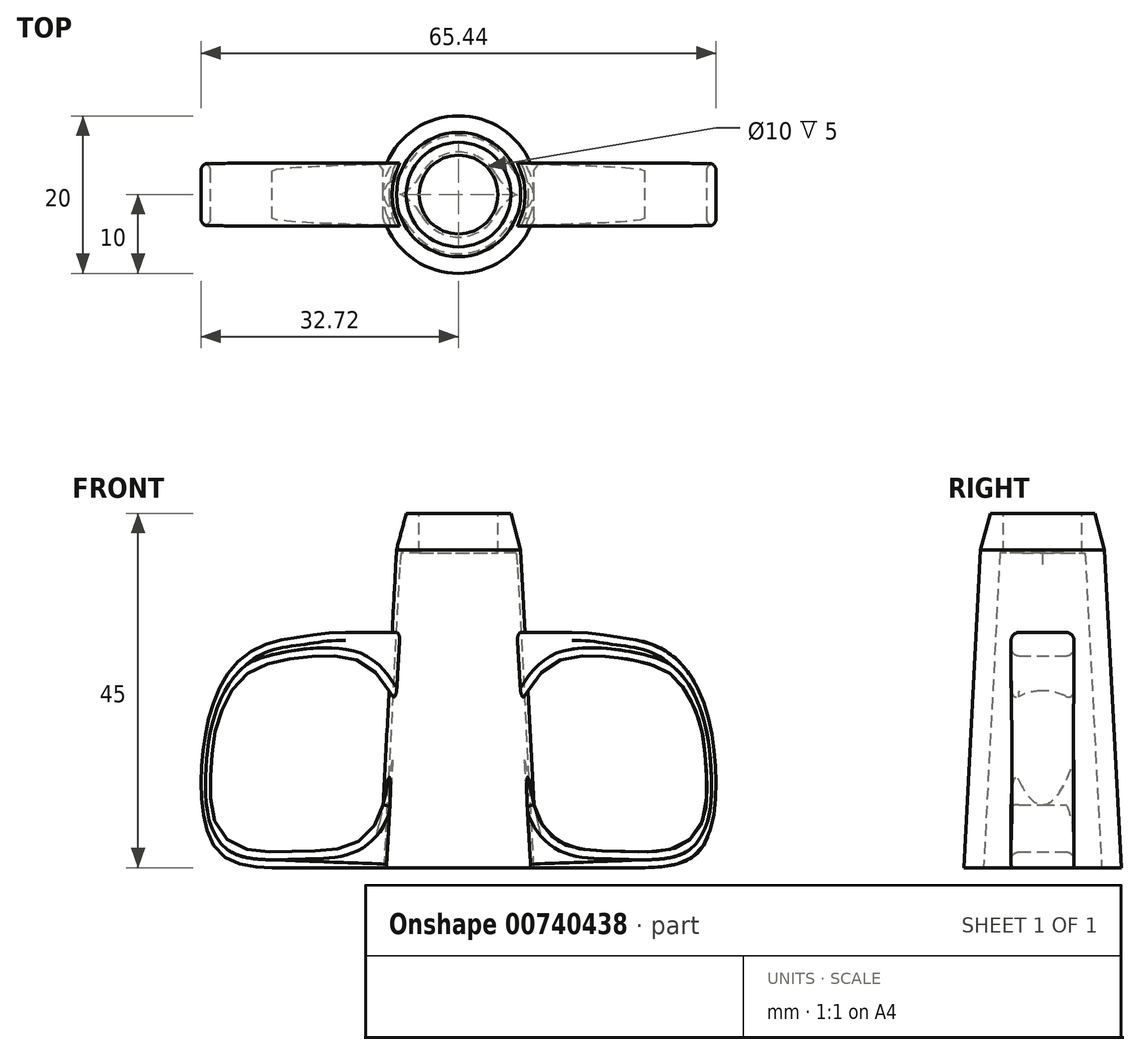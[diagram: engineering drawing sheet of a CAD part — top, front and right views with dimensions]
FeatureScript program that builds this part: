
annotation { "Feature Type Name" : "Feature", "Feature Type Description" : "" }
export const myFeature = defineFeature(function(context is Context, id is Id, definition is map)
    precondition{}
    {
        {
            var Q0;
            Q0=qCreatedBy(makeId("Top.planeOp"),FACE);
            var sketch = newSketch(context, id + "F0", { "sketchPlane" : qUnion([Q0])});
            skCircle(sketch, "E0", {"center": v(0, 0) * mm, "radius": 10 * mm});
            skSolve(sketch);
        }
        {
            var Q0;
            Q0=makeQuery(id+"F0.imprint","IMPRINT",FACE,{"disambiguationData":[TD([[makeQuery(id+"F0.imprint","IMPRINT",EDGE,{"derivedFrom":sQuery(id+"F0.wireOp",EDGE,"E0")}),1.0]])]});
            extrude(context, id + "F1", {"entities" : qUnion([Q0]), "depth" : 45 * mm, "offsetDistance" : 25 * mm, "hasDraft" : true, "draftAngle" : 3 * degree, "draftPullDirection" : true});
        }
        {
            var Q0;
            Q0=makeQuery(id+"F1.opExtrude","CAP_EDGE",EDGE,{"disambiguationData":[OSD([sQuery(id+"F0.wireOp",EDGE,"E0")])],"isStart":false});
            chamfer(context, id + "F2", {"entities" : qUnion([Q0]), "chamferType" : ChamferType.OFFSET_ANGLE, "width" : 1 * mm, "oppositeDirection" : false, "angle" : 75 * degree, "tangentPropagation" : true});
        }
        {
            var Q0;
            Q0=qCreatedBy(makeId("Front.planeOp"),FACE);
            var sketch = newSketch(context, id + "F3", { "sketchPlane" : qUnion([Q0])});
            skLineSegment(sketch, "E1", {"start": v(0, 29.87) * mm, "end": v(14.39, 29.87) * mm});
            skLineSegment(sketch, "E2", {"start": v(0, 0) * mm, "end": v(23.68, 0) * mm});
            skFitSpline(sketch, "E3", {"points": [v(23.68, 0) * mm, v(31, 2.65) * mm, v(31, 21.31) * mm, v(24.85, 28.26) * mm, v(19.65, 29.36) * mm, v(14.39, 29.87) * mm], "startDerivative": vector(45.16, 1.75) * mm, "endDerivative": vector(-49.3, 0) * mm});
            skFitSpline(sketch, "E4", {"points": [v(8.82, 22.47) * mm, v(13.14, 26.44) * mm, v(23.97, 25.92) * mm, v(27.85, 23.73) * mm, v(30.63, 18.39) * mm, v(31.5, 11.29) * mm, v(30.92, 5.73) * mm, v(27.56, 2.5) * mm, v(20.31, 2.07) * mm, v(13.43, 2.95) * mm, v(10.36, 5.87) * mm, v(9.58, 8) * mm], "startDerivative": vector(35.31, 53.22) * mm, "endDerivative": vector(-9.2, 33.37) * mm});
            skLineSegment(sketch, "E5", {"start": v(0, 0) * mm, "end": v(0, 29.87) * mm});
            skLineSegment(sketch, "E6", {"start": v(8.82, 22.47) * mm, "end": v(6.76, 19.38) * mm});
            skLineSegment(sketch, "E7", {"start": v(6.76, 19.38) * mm, "end": v(6.76, 14.55) * mm});
            skLineSegment(sketch, "E8", {"start": v(6.76, 14.55) * mm, "end": v(8.2, 14.55) * mm});
            skLineSegment(sketch, "E9", {"start": v(8.2, 14.55) * mm, "end": v(9.58, 8) * mm});
            skLineSegment(sketch, "E10.MirrorCS", {"start": v(0, 29.87) * mm, "end": v(-14.39, 29.87) * mm});
            skFitSpline(sketch, "E11.MirrorCS", {"points": [v(-23.68, 0) * mm, v(-31, 2.65) * mm, v(-31, 21.31) * mm, v(-24.85, 28.26) * mm, v(-19.65, 29.36) * mm, v(-14.39, 29.87) * mm], "startDerivative": vector(-45.16, 1.75) * mm, "endDerivative": vector(49.3, 0) * mm});
            skFitSpline(sketch, "E12.MirrorCS", {"points": [v(-8.82, 22.47) * mm, v(-13.14, 26.44) * mm, v(-23.97, 25.92) * mm, v(-27.85, 23.73) * mm, v(-30.63, 18.39) * mm, v(-31.5, 11.29) * mm, v(-30.92, 5.73) * mm, v(-27.56, 2.5) * mm, v(-20.31, 2.07) * mm, v(-13.43, 2.95) * mm, v(-10.36, 5.87) * mm, v(-9.58, 8) * mm], "startDerivative": vector(-35.31, 53.22) * mm, "endDerivative": vector(9.2, 33.37) * mm});
            skLineSegment(sketch, "E13.MirrorCS", {"start": v(-8.82, 22.47) * mm, "end": v(-6.76, 19.38) * mm});
            skLineSegment(sketch, "E14.MirrorCS", {"start": v(-6.76, 19.38) * mm, "end": v(-6.76, 14.55) * mm});
            skLineSegment(sketch, "E15.MirrorCS", {"start": v(-8.2, 14.55) * mm, "end": v(-9.58, 8) * mm});
            skLineSegment(sketch, "E16.MirrorCS", {"start": v(-6.76, 14.55) * mm, "end": v(-8.2, 14.55) * mm});
            skLineSegment(sketch, "E17.MirrorCS", {"start": v(0, 0) * mm, "end": v(-23.68, 0) * mm});
            skSolve(sketch);
        }
        {
            var Q0;
            Q0=makeQuery(id+"F3.imprint","IMPRINT",FACE,{"disambiguationData":[TD([[makeQuery(id+"F3.imprint","IMPRINT",EDGE,{"derivedFrom":sQuery(id+"F3.wireOp",EDGE,"E1")}),-1.0]])]});
            var Q1;
            Q1=makeQuery(id+"F3.imprint","IMPRINT",FACE,{"disambiguationData":[TD([[makeQuery(id+"F3.imprint","IMPRINT",EDGE,{"derivedFrom":sQuery(id+"F3.wireOp",EDGE,"E5")}),1.0]])]});
            extrude(context, id + "F4", {"entities" : qUnion([Q0, Q1]), "operationType" : NewBodyOperationType.ADD, "depth" : 4 * mm, "offsetDistance" : 25 * mm, "hasSecondDirection" : true, "secondDirectionOppositeDirection" : true, "secondDirectionDepth" : 4 * mm});
        }
        {
            var Q0;
            Q0=makeQuery(id+"F4.opExtrude","CAP_EDGE",EDGE,{"disambiguationData":[OSD([sQuery(id+"F3.wireOp",EDGE,"E11.MirrorCS")])],"isStart":false});
            var Q1;
            Q1=makeQuery(id+"F4.opExtrude","CAP_EDGE",EDGE,{"disambiguationData":[OSD([sQuery(id+"F3.wireOp",EDGE,"E12.MirrorCS")])],"isStart":false});
            var Q2;
            Q2=makeQuery(id+"F4.opExtrude","CAP_EDGE",EDGE,{"disambiguationData":[OSD([sQuery(id+"F3.wireOp",EDGE,"E15.MirrorCS")])],"isStart":false});
            var Q3;
            Q3=makeQuery(id+"F4.opExtrude","CAP_EDGE",EDGE,{"disambiguationData":[OSD([sQuery(id+"F3.wireOp",EDGE,"E4")])],"isStart":false});
            var Q4;
            Q4=makeQuery(id+"F4.opExtrude","CAP_EDGE",EDGE,{"disambiguationData":[OSD([sQuery(id+"F3.wireOp",EDGE,"E9")])],"isStart":false});
            var Q5;
            {var subQ0=sQuery(id+"F3.wireOp",EDGE,"E10.MirrorCS");var subQ1=sQuery(id+"F3.wireOp",EDGE,"E3");var subQ2=sQuery(id+"F3.wireOp",EDGE,"E1");Q5=makeQuery(id+"F4.boolean.opBoolean","SPLIT",EDGE,{"disambiguationData":[TD([makeQuery(id+"F4.opExtrude","SWEPT_FACE",FACE,{"disambiguationData":[OSD([subQ1])]})])],"derivedFrom":makeQuery(id+"F4.opExtrude","CAP_EDGE",EDGE,{"disambiguationData":[OSD([subQ2,subQ0])],"isStart":false})});}
            var Q6;
            Q6=makeQuery(id+"F4.opExtrude","CAP_EDGE",EDGE,{"disambiguationData":[OSD([sQuery(id+"F3.wireOp",EDGE,"E3")])],"isStart":false});
            var Q7;
            Q7=makeQuery(id+"F4.opExtrude","CAP_EDGE",EDGE,{"disambiguationData":[OSD([sQuery(id+"F3.wireOp",EDGE,"E3")])],"isStart":true});
            var Q8;
            Q8=makeQuery(id+"F4.opExtrude","CAP_EDGE",EDGE,{"disambiguationData":[OSD([sQuery(id+"F3.wireOp",EDGE,"E11.MirrorCS")])],"isStart":true});
            var Q9;
            Q9=makeQuery(id+"F4.opExtrude","CAP_EDGE",EDGE,{"disambiguationData":[OSD([sQuery(id+"F3.wireOp",EDGE,"E12.MirrorCS")])],"isStart":true});
            var Q10;
            Q10=makeQuery(id+"F4.opExtrude","CAP_EDGE",EDGE,{"disambiguationData":[OSD([sQuery(id+"F3.wireOp",EDGE,"E4")])],"isStart":true});
            fillet(context, id + "F5", {"entities" : qUnion([Q0, Q1, Q2, Q3, Q4, Q5, Q6, Q7, Q8, Q9, Q10]), "radius" : 1 * mm, "tangentPropagation" : true, "allowEdgeOverflow" : false});
        }
        {
            var Q0;
            Q0=makeQuery(id+"F4.boolean.opBoolean","MERGE",FACE,{"derivedFrom":[makeQuery(id+"F1.opExtrude","CAP_FACE",FACE,{"disambiguationData":[OSD([sQuery(id+"F0.wireOp",EDGE,"E0")])],"isStart":true}),makeQuery(id+"F4.opExtrude","SWEPT_FACE",FACE,{"disambiguationData":[OSD([sQuery(id+"F3.wireOp",EDGE,"E2"),sQuery(id+"F3.wireOp",EDGE,"E17.MirrorCS")])]})]});
            var sketch = newSketch(context, id + "F6", { "sketchPlane" : qUnion([Q0])});
            skArc(sketch, "E18", {"start": v(-6.54, -3.67) * mm, "mid": v(0, -7.5) * mm, "end": v(6.54, -3.67) * mm});
            skArc(sketch, "E19", {"start": v(-8.47, 1.75) * mm, "mid": v(-9.5, 0) * mm, "end": v(-8.47, -1.75) * mm});
            skArc(sketch, "E20", {"start": v(8.47, -1.75) * mm, "mid": v(9.5, 0) * mm, "end": v(8.47, 1.75) * mm});
            skArc(sketch, "E21.trimOffspring", {"start": v(6.54, 3.67) * mm, "mid": v(0, 7.5) * mm, "end": v(-6.54, 3.67) * mm});
            skPoint(sketch, "E22.visualSharp", {"position": v(-7.23, 1.98) * mm});
            skArc(sketch, "E22.filletArc", {"start": v(-8.47, 1.75) * mm, "mid": v(-7.37, 2.58) * mm, "end": v(-6.54, 3.67) * mm});
            skPoint(sketch, "E23.visualSharp", {"position": v(-7.23, -1.98) * mm});
            skArc(sketch, "E23.filletArc", {"start": v(-6.54, -3.67) * mm, "mid": v(-7.37, -2.58) * mm, "end": v(-8.47, -1.75) * mm});
            skPoint(sketch, "E24.visualSharp", {"position": v(7.23, -1.98) * mm});
            skArc(sketch, "E24.filletArc", {"start": v(8.47, -1.75) * mm, "mid": v(7.37, -2.58) * mm, "end": v(6.54, -3.67) * mm});
            skPoint(sketch, "E25.visualSharp", {"position": v(7.23, 1.98) * mm});
            skArc(sketch, "E25.filletArc", {"start": v(6.54, 3.67) * mm, "mid": v(7.37, 2.58) * mm, "end": v(8.47, 1.75) * mm});
            skSolve(sketch);
        }
        {
            var Q0;
            Q0=makeQuery(id+"F6.imprint","IMPRINT",FACE,{"disambiguationData":[TD([[makeQuery(id+"F6.imprint","IMPRINT",EDGE,{"derivedFrom":sQuery(id+"F6.wireOp",EDGE,"E18")}),1.0]])]});
            extrude(context, id + "F7", {"entities" : qUnion([Q0]), "operationType" : NewBodyOperationType.REMOVE, "oppositeDirection" : true, "depth" : 40 * mm, "offsetDistance" : 25 * mm, "hasDraft" : true, "draftAngle" : 3 * degree, "draftPullDirection" : true});
        }
        {
            var Q0;
            Q0=makeQuery(id+"F1.opExtrude","CAP_FACE",FACE,{"disambiguationData":[OSD([sQuery(id+"F0.wireOp",EDGE,"E0")])],"isStart":false});
            var sketch = newSketch(context, id + "F8", { "sketchPlane" : qUnion([Q0])});
            skCircle(sketch, "E26", {"center": v(0, 0) * mm, "radius": 5 * mm});
            skSolve(sketch);
        }
        {
            var Q0;
            Q0=makeQuery(id+"F8.imprint","IMPRINT",FACE,{"disambiguationData":[TD([[makeQuery(id+"F8.imprint","IMPRINT",EDGE,{"derivedFrom":sQuery(id+"F8.wireOp",EDGE,"E26")}),1.0]])]});
            extrude(context, id + "F9", {"entities" : qUnion([Q0]), "operationType" : NewBodyOperationType.REMOVE, "endBound" : BoundingType.UP_TO_NEXT, "oppositeDirection" : true, "depth" : 25 * mm, "offsetDistance" : 25 * mm});
        }
    });
